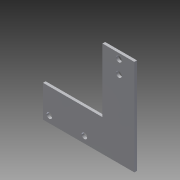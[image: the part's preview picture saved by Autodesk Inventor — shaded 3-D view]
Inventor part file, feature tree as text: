
AUTODESK INVENTOR PART (.ipt)
format: ipt  version: 2013 (Build 170138000, 138)  size: 146,432 bytes
history: native  units: in
note: dims shown in document units (in); Inventor stores cm internally (conversion verified against a paired STEP export)
features: sketch x6, other x5, reference x4, extrude x2, sheet_metal_op x1
ambient origin geometry x8: Origin, YZ Plane, XZ Plane, XY Plane, X Axis, Y Axis, Z Axis, Center Point
bodies: Solid1 (feature_tree)
feature tree (18):
  sheet_metal_op  "Face1"
  extrude  "Extrusion1"  Depth=1.5in
  extrude  "Extrusion2"  Depth=1.181in
  sketch  "Sketch1"  dims[d1=2.244in d2=1.5in]
  other  "Plate1"
  sketch  "Sketch8"  dims[d3=0.295in d4=1.181in]
  reference  "Reference1"
  reference  "Reference2"
  sketch  "Sketch10"  dims[d5=0.295in]
  sketch  "Sketch13"  dims[d8=0.125in]
  sketch  "Sketch14"  dims[d19=0.125in]
  reference  "Reference7"
  reference  "Reference8"
  sketch  "Sketch15"  dims[d20=0.0in d21=2.053in d22=0.0in d27=3.0in d28=0.0in d29=0.125in d30=0.0in d31=1.5in d32=0.125in d33=0.0in]
  other  "Cut1"
  other  "Cut4"
  other  "Cut5"
  other  "Definition1"
